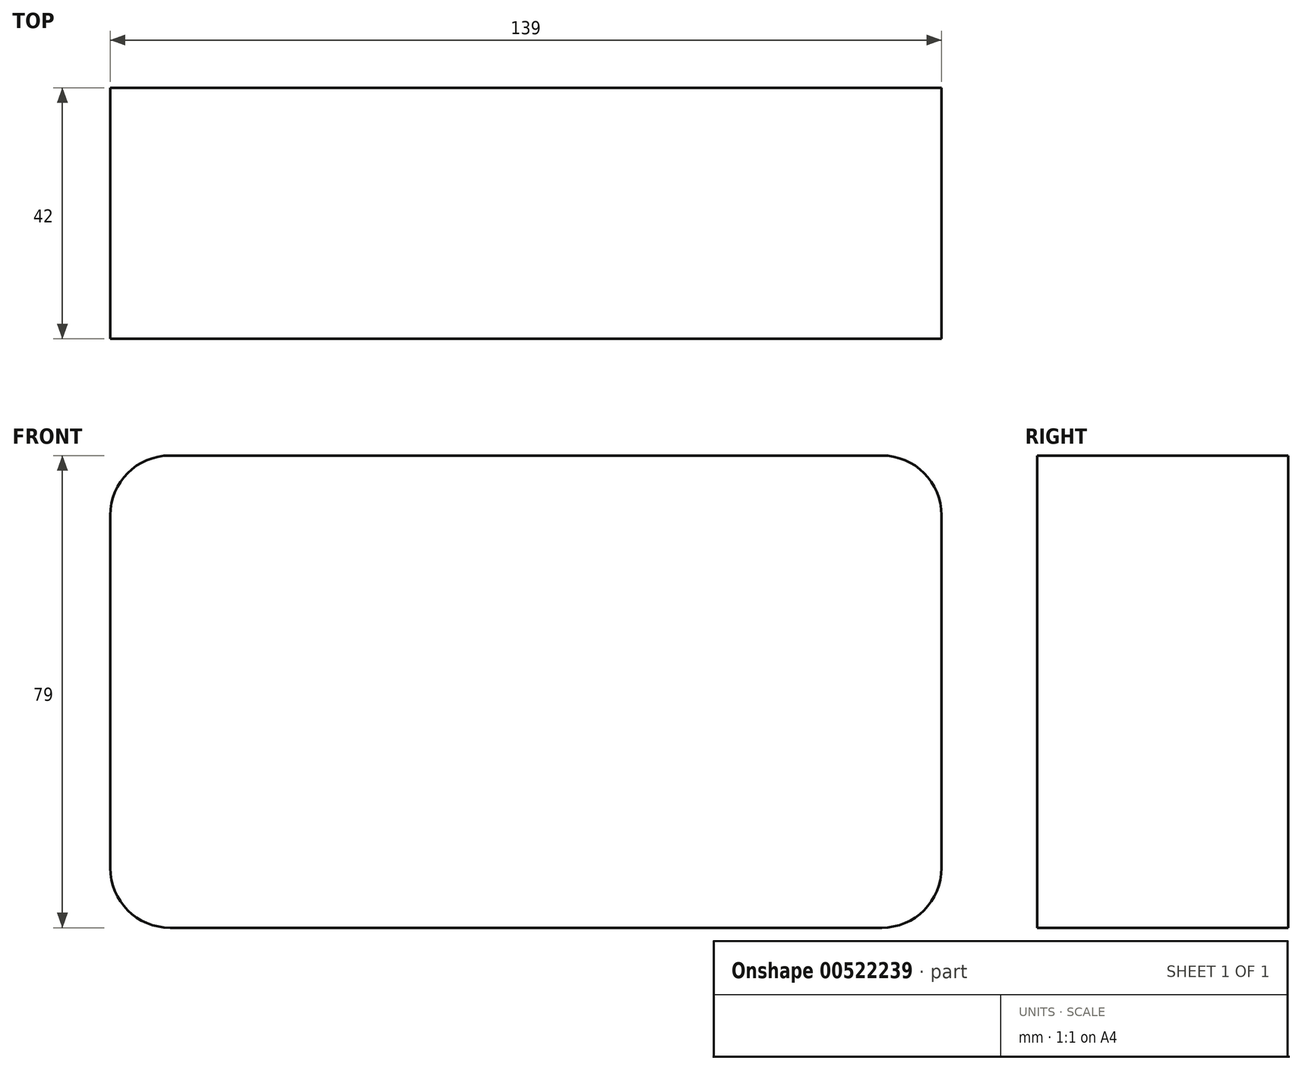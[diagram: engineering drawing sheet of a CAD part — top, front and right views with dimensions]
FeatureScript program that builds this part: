
annotation { "Feature Type Name" : "Feature", "Feature Type Description" : "" }
export const myFeature = defineFeature(function(context is Context, id is Id, definition is map)
    precondition{}
    {
        {
            var Q0;
            Q0=qCreatedBy(makeId("Front.planeOp"),FACE);
            var sketch = newSketch(context, id + "F0", { "sketchPlane" : qUnion([Q0])});
            skLineSegment(sketch, "E0.bottom", {"start": v(-53.9, 37.82) * mm, "end": v(65.1, 37.82) * mm});
            skLineSegment(sketch, "E0.top", {"start": v(-53.9, -41.18) * mm, "end": v(65.1, -41.18) * mm});
            skLineSegment(sketch, "E0.left", {"start": v(-63.9, 27.82) * mm, "end": v(-63.9, -31.18) * mm});
            skLineSegment(sketch, "E0.right", {"start": v(75.1, 27.82) * mm, "end": v(75.1, -31.18) * mm});
            skPoint(sketch, "E1.visualSharp", {"position": v(-63.9, 37.82) * mm});
            skArc(sketch, "E1.filletArc", {"start": v(-53.9, 37.82) * mm, "mid": v(-60.98, 34.89) * mm, "end": v(-63.9, 27.82) * mm});
            skPoint(sketch, "E2.visualSharp", {"position": v(-63.9, -41.18) * mm});
            skArc(sketch, "E2.filletArc", {"start": v(-63.9, -31.18) * mm, "mid": v(-60.98, -38.26) * mm, "end": v(-53.9, -41.18) * mm});
            skPoint(sketch, "E3.visualSharp", {"position": v(75.1, 37.82) * mm});
            skArc(sketch, "E3.filletArc", {"start": v(75.1, 27.82) * mm, "mid": v(72.16, 34.89) * mm, "end": v(65.1, 37.82) * mm});
            skPoint(sketch, "E4.visualSharp", {"position": v(75.1, -41.18) * mm});
            skArc(sketch, "E4.filletArc", {"start": v(65.1, -41.18) * mm, "mid": v(72.16, -38.26) * mm, "end": v(75.1, -31.18) * mm});
            skSolve(sketch);
        }
        {
            var Q0;
            Q0 = qSketchRegion(id + "F0", true);
            extrude(context, id + "F1", {"entities" : qUnion([Q0]), "depth" : 42 * mm, "offsetDistance" : 25 * mm});
        }
    });
